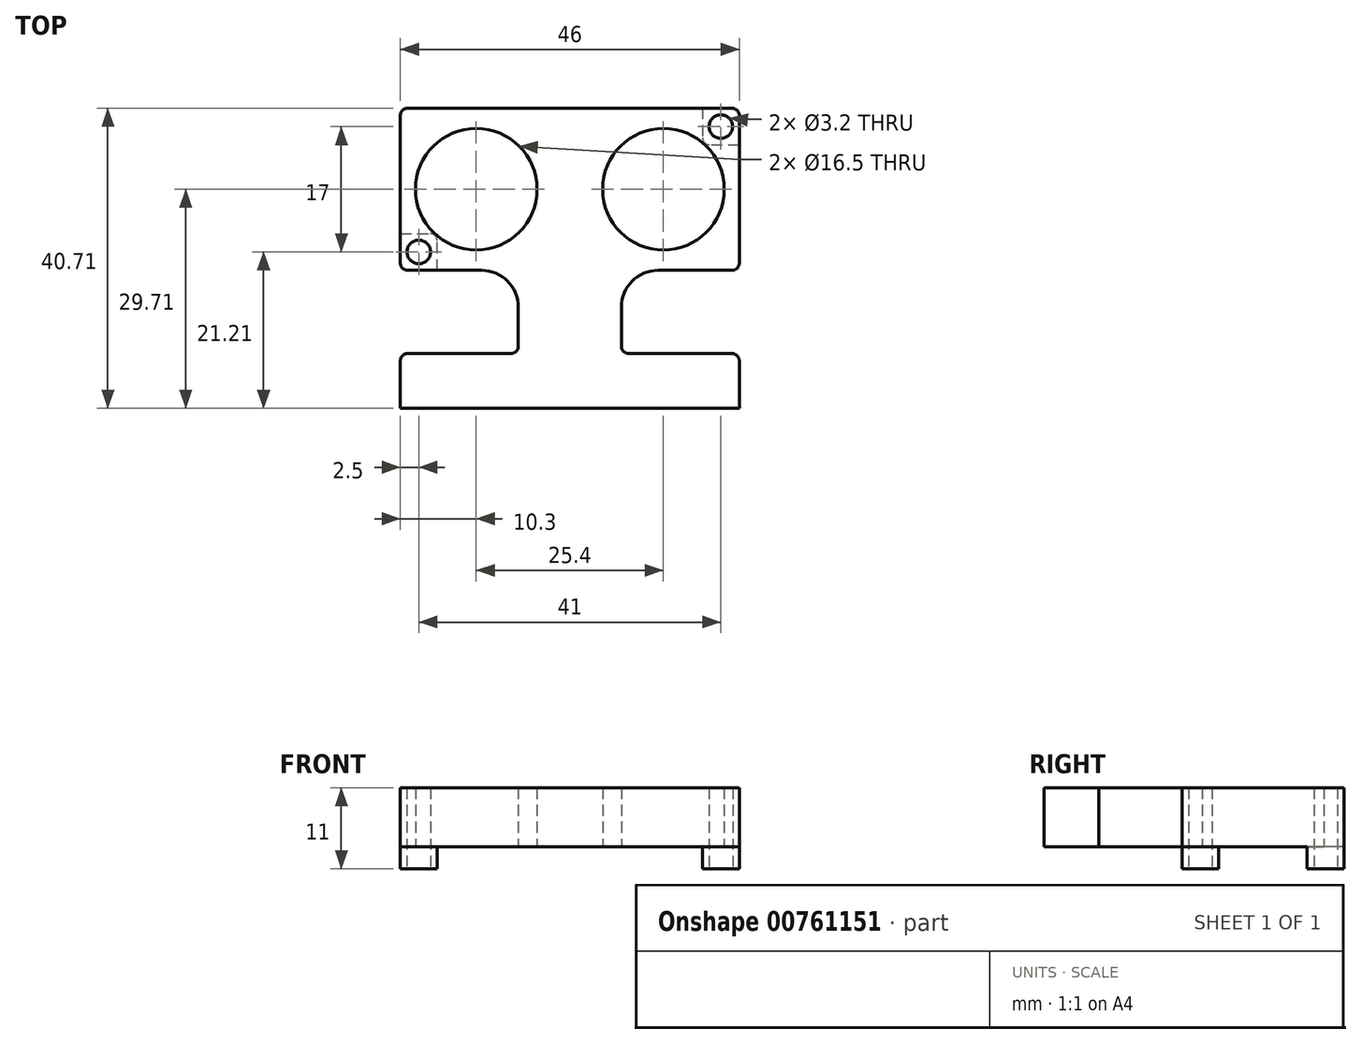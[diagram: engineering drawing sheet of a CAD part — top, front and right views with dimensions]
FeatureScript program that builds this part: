
annotation { "Feature Type Name" : "Feature", "Feature Type Description" : "" }
export const myFeature = defineFeature(function(context is Context, id is Id, definition is map)
    precondition{}
    {
        {
            var Q0;
            Q0=qCreatedBy(makeId("Top.planeOp"),FACE);
            var sketch = newSketch(context, id + "F0", { "sketchPlane" : qUnion([Q0])});
            skPoint(sketch, "E0.middle", {"position": v(0, 0) * mm});
            skCircle(sketch, "E1", {"center": v(-12.7, 0) * mm, "radius": 8.25 * mm});
            skCircle(sketch, "E2.1.0", {"center": v(12.7, 0) * mm, "radius": 8.25 * mm});
            skCircle(sketch, "E3", {"center": v(20.5, 8.5) * mm, "radius": 1.6 * mm});
            skCircle(sketch, "E4", {"center": v(-20.5, -8.5) * mm, "radius": 1.6 * mm});
            skLineSegment(sketch, "E5.top", {"start": v(23, -29.7) * mm, "end": v(-23, -29.7) * mm});
            skLineSegment(sketch, "E5.left", {"start": v(23, -23.3) * mm, "end": v(23, -29.7) * mm});
            skLineSegment(sketch, "E5.right", {"start": v(-23, -23.3) * mm, "end": v(-23, -29.7) * mm});
            skPoint(sketch, "E5.middle", {"position": v(0, -26) * mm});
            skLineSegment(sketch, "E6", {"start": v(-7, -21.3) * mm, "end": v(-7, -16) * mm});
            skLineSegment(sketch, "E7", {"start": v(-22, -22.3) * mm, "end": v(-8, -22.3) * mm});
            skLineSegment(sketch, "E8", {"start": v(8, -22.3) * mm, "end": v(22, -22.3) * mm});
            skLineSegment(sketch, "E9", {"start": v(7, -21.3) * mm, "end": v(7, -16) * mm});
            skLineSegment(sketch, "E10", {"start": v(12, -11) * mm, "end": v(22, -11) * mm});
            skPoint(sketch, "E11.visualSharp", {"position": v(-23, 11) * mm});
            skArc(sketch, "E11.filletArc", {"start": v(-22, 11) * mm, "mid": v(-22.7, 10.7) * mm, "end": v(-23, 10) * mm});
            skPoint(sketch, "E12.visualSharp", {"position": v(-7, -11) * mm});
            skArc(sketch, "E12.filletArc", {"start": v(-7, -16) * mm, "mid": v(-8.46, -12.46) * mm, "end": v(-12, -11) * mm});
            skPoint(sketch, "E13.visualSharp", {"position": v(7, -11) * mm});
            skArc(sketch, "E13.filletArc", {"start": v(12, -11) * mm, "mid": v(8.46, -12.46) * mm, "end": v(7, -16) * mm});
            skPoint(sketch, "E14.visualSharp", {"position": v(23, -11) * mm});
            skArc(sketch, "E14.filletArc", {"start": v(22, -11) * mm, "mid": v(22.7, -10.7) * mm, "end": v(23, -10) * mm});
            skPoint(sketch, "E15.visualSharp", {"position": v(-23, -22.3) * mm});
            skArc(sketch, "E15.filletArc", {"start": v(-22, -22.3) * mm, "mid": v(-22.7, -22.58) * mm, "end": v(-23, -23.3) * mm});
            skPoint(sketch, "E16.visualSharp", {"position": v(23, -22.3) * mm});
            skArc(sketch, "E16.filletArc", {"start": v(23, -23.3) * mm, "mid": v(22.7, -22.58) * mm, "end": v(22, -22.3) * mm});
            skPoint(sketch, "E17.visualSharp", {"position": v(-7, -22.3) * mm});
            skArc(sketch, "E17.filletArc", {"start": v(-8, -22.3) * mm, "mid": v(-7.3, -22) * mm, "end": v(-7, -21.3) * mm});
            skPoint(sketch, "E18.visualSharp", {"position": v(7, -22.3) * mm});
            skArc(sketch, "E18.filletArc", {"start": v(7, -21.3) * mm, "mid": v(7.3, -22) * mm, "end": v(8, -22.3) * mm});
            skLineSegment(sketch, "E19.bottom", {"start": v(-22, -11) * mm, "end": v(-18, -11) * mm});
            skLineSegment(sketch, "E19.top", {"start": v(-23, -6) * mm, "end": v(-19, -6) * mm});
            skLineSegment(sketch, "E19.left", {"start": v(-23, -10) * mm, "end": v(-23, -6) * mm});
            skLineSegment(sketch, "E19.right", {"start": v(-18, -11) * mm, "end": v(-18, -7) * mm});
            skPoint(sketch, "E20.visualSharp", {"position": v(-18, -6) * mm});
            skArc(sketch, "E20.filletArc", {"start": v(-18, -7) * mm, "mid": v(-18.3, -6.3) * mm, "end": v(-19, -6) * mm});
            skPoint(sketch, "E21.visualSharp", {"position": v(-23, -11) * mm});
            skArc(sketch, "E21.filletArc", {"start": v(-23, -10) * mm, "mid": v(-22.7, -10.7) * mm, "end": v(-22, -11) * mm});
            skLineSegment(sketch, "E22", {"start": v(-23, 10) * mm, "end": v(-23, -6) * mm});
            skLineSegment(sketch, "E23", {"start": v(-18, -11) * mm, "end": v(-12, -11) * mm});
            skLineSegment(sketch, "E24.bottom", {"start": v(22, 11) * mm, "end": v(18, 11) * mm});
            skLineSegment(sketch, "E24.top", {"start": v(23, 6) * mm, "end": v(19, 6) * mm});
            skLineSegment(sketch, "E24.left", {"start": v(23, 10) * mm, "end": v(23, 6) * mm});
            skLineSegment(sketch, "E24.right", {"start": v(18, 11) * mm, "end": v(18, 7) * mm});
            skPoint(sketch, "E25.visualSharp", {"position": v(18, 6) * mm});
            skArc(sketch, "E25.filletArc", {"start": v(18, 7) * mm, "mid": v(18.3, 6.3) * mm, "end": v(19, 6) * mm});
            skPoint(sketch, "E26.visualSharp", {"position": v(23, 11) * mm});
            skArc(sketch, "E26.filletArc", {"start": v(23, 10) * mm, "mid": v(22.7, 10.7) * mm, "end": v(22, 11) * mm});
            skLineSegment(sketch, "E27", {"start": v(-22, 11) * mm, "end": v(18, 11) * mm});
            skLineSegment(sketch, "E28", {"start": v(23, 6) * mm, "end": v(23, -10) * mm});
            skSolve(sketch);
        }
        {
            var Q0;
            Q0=makeQuery(id+"F0.imprint","IMPRINT",FACE,{"disambiguationData":[TD([[makeQuery(id+"F0.imprint","IMPRINT",EDGE,{"derivedFrom":sQuery(id+"F0.wireOp",EDGE,"E1")}),-1.0]])]});
            var Q1;
            Q1=makeQuery(id+"F0.imprint","IMPRINT",FACE,{"disambiguationData":[TD([[makeQuery(id+"F0.imprint","IMPRINT",EDGE,{"derivedFrom":sQuery(id+"F0.wireOp",EDGE,"E3")}),-1.0]])]});
            var Q2;
            Q2=makeQuery(id+"F0.imprint","IMPRINT",FACE,{"disambiguationData":[TD([[makeQuery(id+"F0.imprint","IMPRINT",EDGE,{"derivedFrom":sQuery(id+"F0.wireOp",EDGE,"E4")}),-1.0]])]});
            extrude(context, id + "F1", {"entities" : qUnion([Q0, Q1, Q2]), "depth" : 8 * mm, "offsetDistance" : 25 * mm});
        }
        {
            var Q0;
            Q0=makeQuery(id+"F0.imprint","IMPRINT",FACE,{"disambiguationData":[TD([[makeQuery(id+"F0.imprint","IMPRINT",EDGE,{"derivedFrom":sQuery(id+"F0.wireOp",EDGE,"E4")}),-1.0]])]});
            var Q1;
            Q1=makeQuery(id+"F0.imprint","IMPRINT",FACE,{"disambiguationData":[TD([[makeQuery(id+"F0.imprint","IMPRINT",EDGE,{"derivedFrom":sQuery(id+"F0.wireOp",EDGE,"E3")}),-1.0]])]});
            extrude(context, id + "F2", {"entities" : qUnion([Q0, Q1]), "operationType" : NewBodyOperationType.ADD, "oppositeDirection" : true, "depth" : 3 * mm, "offsetDistance" : 25 * mm});
        }
    });
